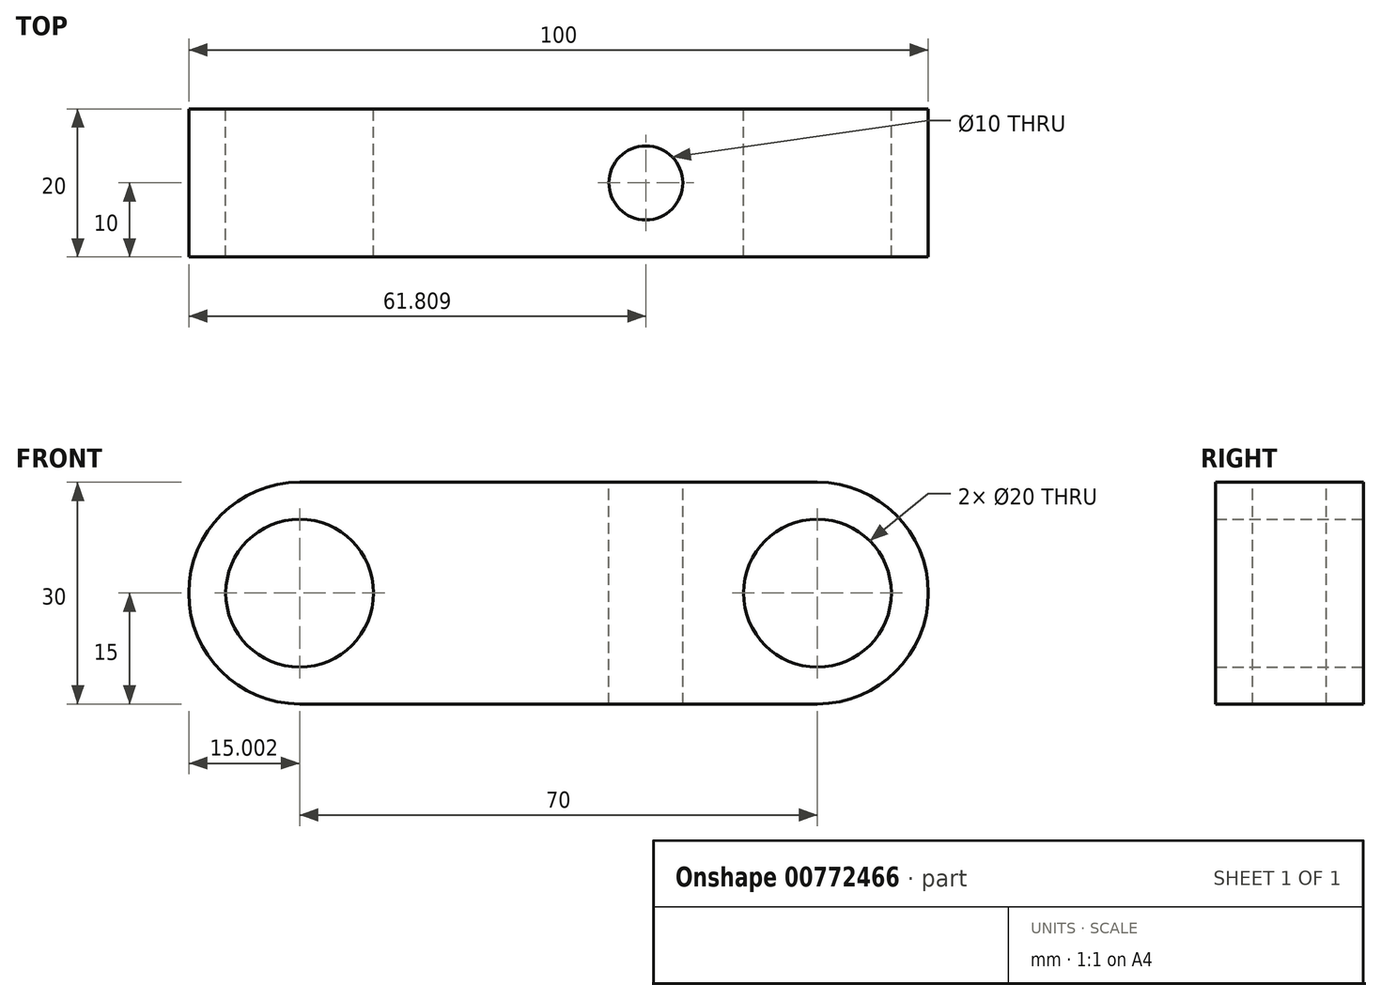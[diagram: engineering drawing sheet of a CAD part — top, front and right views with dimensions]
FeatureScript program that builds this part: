
annotation { "Feature Type Name" : "Feature", "Feature Type Description" : "" }
export const myFeature = defineFeature(function(context is Context, id is Id, definition is map)
    precondition{}
    {
        {
            var Q0;
            Q0=qCreatedBy(makeId("Front.planeOp"),FACE);
            var sketch = newSketch(context, id + "F0", { "sketchPlane" : qUnion([Q0])});
            skPoint(sketch, "E0.centerSnap0", {"position": v(-36.8, -0.08) * mm});
            skCircle(sketch, "E1", {"center": v(-36.8, 0) * mm, "radius": 10 * mm});
            skCircle(sketch, "E2", {"center": v(33.2, 0) * mm, "radius": 10 * mm});
            skArc(sketch, "E3.0", {"start": v(-36.8, 15) * mm, "mid": v(-51.8, 0) * mm, "end": v(-36.8, -15) * mm});
            skArc(sketch, "E4.0", {"start": v(33.2, -15) * mm, "mid": v(48.2, 0) * mm, "end": v(33.2, 15) * mm});
            skLineSegment(sketch, "E5", {"start": v(-36.8, 0) * mm, "end": v(-36.8, -0.08) * mm});
            skLineSegment(sketch, "E6", {"start": v(33.2, -15) * mm, "end": v(-36.8, -15) * mm});
            skLineSegment(sketch, "E7", {"start": v(33.2, 15) * mm, "end": v(-36.8, 15) * mm});
            skPoint(sketch, "E8", {"position": v(7.56, 0) * mm});
            skPoint(sketch, "E9.orphan", {"position": v(7.56, 15) * mm});
            skPoint(sketch, "E10.end.orphan", {"position": v(7.56, -15) * mm});
            skSolve(sketch);
        }
        {
            var Q0;
            Q0 = qSketchRegion(id + "F0", true);
            extrude(context, id + "F1", {"entities" : qUnion([Q0]), "depth" : 20 * mm, "offsetDistance" : 25 * mm});
        }
        {
            var Q0;
            Q0=makeQuery(id+"F1.opExtrude","SWEPT_FACE",FACE,{"disambiguationData":[OSD([sQuery(id+"F0.wireOp",EDGE,"E7")])]});
            var sketch = newSketch(context, id + "F2", { "sketchPlane" : qUnion([Q0])});
            skPoint(sketch, "E11", {"position": v(10, -10) * mm});
            skSolve(sketch);
        }
        {
            var Q0;
            Q0=sQuery(id+"F2.wireOp",VERTEX,"E11");
            var Q1;
            Q1=makeQuery(id+"F1.opExtrude","SWEPT_BODY",BODY,{"disambiguationData":[OSD([sQuery(id+"F0.wireOp",EDGE,"E1"),sQuery(id+"F0.wireOp",EDGE,"E2"),sQuery(id+"F0.wireOp",EDGE,"E3.0"),sQuery(id+"F0.wireOp",EDGE,"E4.0"),sQuery(id+"F0.wireOp",EDGE,"E6"),sQuery(id+"F0.wireOp",EDGE,"E7")])]});
            hole(context, id + "F3", {"style" : HoleStyle.SIMPLE, "endStyle" : HoleEndStyle.THROUGH, "holeDiameter" : 10 * mm, "majorDiameter" : 5 * mm, "isTappedThrough" : true, "tappedDepth" : 12 * mm, "tapClearance" : 3, "locations" : qUnion([Q0]), "scope" : qUnion([Q1])});
        }
    });
